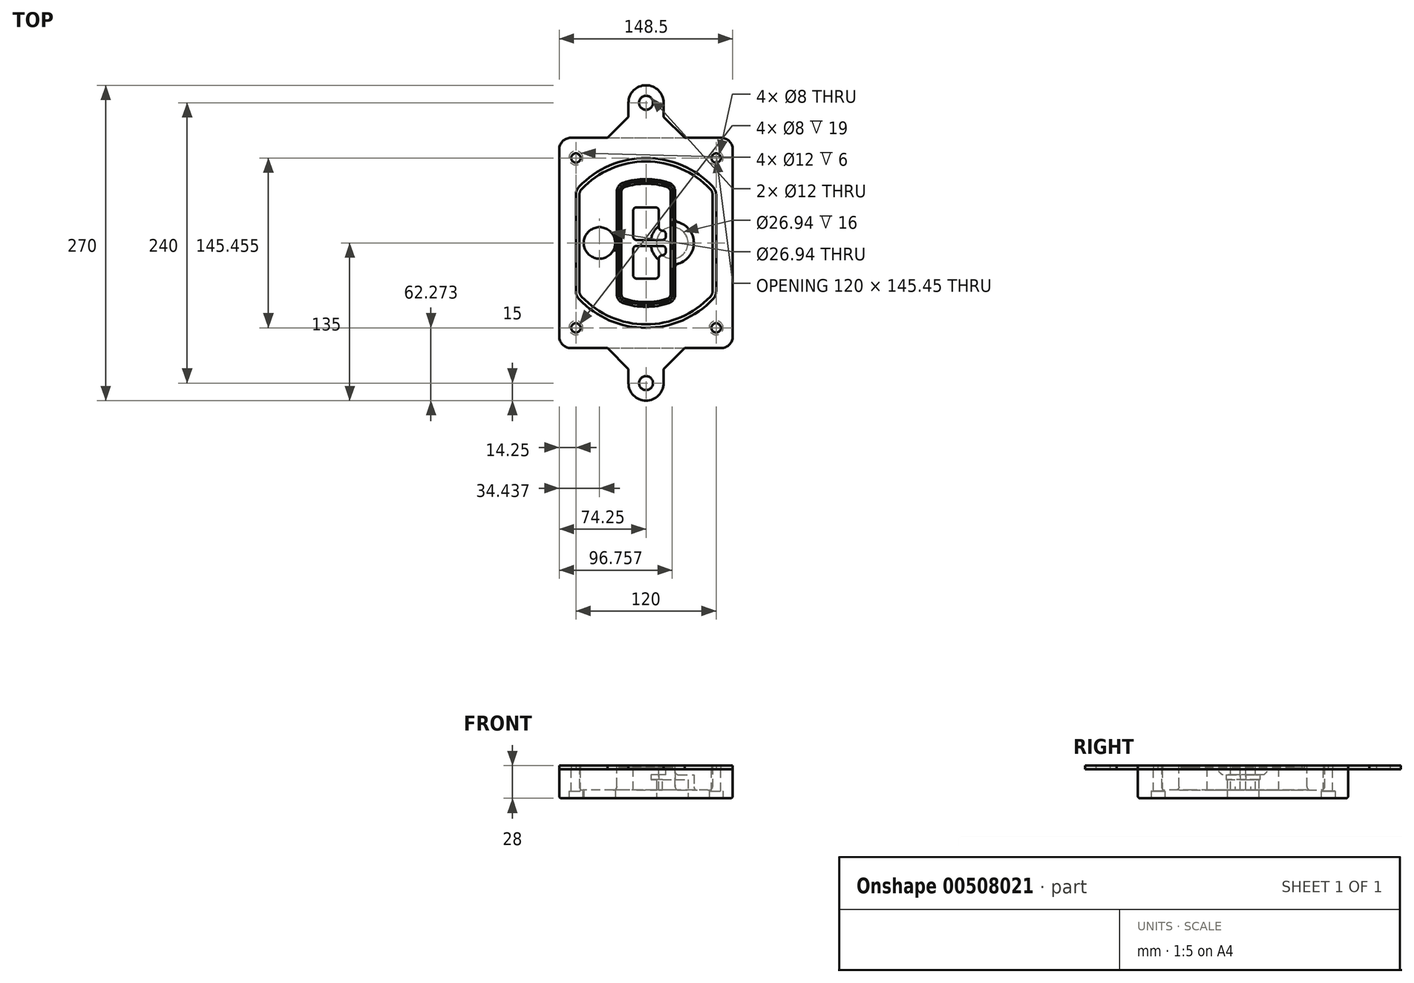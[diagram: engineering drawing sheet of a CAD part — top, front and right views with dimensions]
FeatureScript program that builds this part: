
annotation { "Feature Type Name" : "Feature", "Feature Type Description" : "" }
export const myFeature = defineFeature(function(context is Context, id is Id, definition is map)
    precondition{}
    {
        {
            var Q0;
            Q0=qCreatedBy(makeId("Top.planeOp"),FACE);
            var sketch = newSketch(context, id + "F0", { "sketchPlane" : qUnion([Q0])});
            skPoint(sketch, "E0.rect.middle", {"position": v(0, 0) * mm});
            skLineSegment(sketch, "E1.bottom", {"start": v(-64.25, -90) * mm, "end": v(64.25, -90) * mm});
            skLineSegment(sketch, "E1.top", {"start": v(-64.25, 90) * mm, "end": v(64.25, 90) * mm});
            skLineSegment(sketch, "E1.left", {"start": v(-74.25, -80) * mm, "end": v(-74.25, 80) * mm});
            skLineSegment(sketch, "E1.right", {"start": v(74.25, -80) * mm, "end": v(74.25, 80) * mm});
            skLineSegment(sketch, "E2", {"start": v(-74.25, 90) * mm, "end": v(74.25, -90) * mm, "construction": true});
            skLineSegment(sketch, "E3", {"start": v(74.25, 90) * mm, "end": v(-74.25, -90) * mm, "construction": true});
            skCircle(sketch, "E4", {"center": v(-60, 72.73) * mm, "radius": 4 * mm});
            skCircle(sketch, "E5", {"center": v(60, 72.73) * mm, "radius": 4 * mm});
            skCircle(sketch, "E6", {"center": v(60, -72.73) * mm, "radius": 4 * mm});
            skCircle(sketch, "E7", {"center": v(-60, -72.73) * mm, "radius": 4 * mm});
            skLineSegment(sketch, "E8", {"start": v(-60, 72.73) * mm, "end": v(60, 72.73) * mm, "construction": true});
            skLineSegment(sketch, "E9", {"start": v(60, 72.73) * mm, "end": v(60, -72.73) * mm, "construction": true});
            skLineSegment(sketch, "E10", {"start": v(60, -72.73) * mm, "end": v(-60, -72.73) * mm, "construction": true});
            skLineSegment(sketch, "E11", {"start": v(-60, -72.73) * mm, "end": v(-60, 72.73) * mm, "construction": true});
            skLineSegment(sketch, "E12", {"start": v(-60, 41.18) * mm, "end": v(-60, -41.18) * mm});
            skLineSegment(sketch, "E13", {"start": v(60, 41.18) * mm, "end": v(60, -41.18) * mm});
            skArc(sketch, "E14", {"start": v(57.27, 48.05) * mm, "mid": v(0, 72.73) * mm, "end": v(-57.27, 48.05) * mm});
            skArc(sketch, "E15", {"start": v(-57.27, -48.05) * mm, "mid": v(0, -72.73) * mm, "end": v(57.27, -48.05) * mm});
            skLineSegment(sketch, "E16", {"start": v(-60, 0) * mm, "end": v(60, 0) * mm, "construction": true});
            skPoint(sketch, "E17.visualSharp", {"position": v(-60, -45) * mm});
            skArc(sketch, "E17.filletArc", {"start": v(-60, -41.18) * mm, "mid": v(-59.3, -44.87) * mm, "end": v(-57.27, -48.05) * mm});
            skPoint(sketch, "E18.visualSharp", {"position": v(-60, 45) * mm});
            skArc(sketch, "E18.filletArc", {"start": v(-57.27, 48.05) * mm, "mid": v(-59.3, 44.87) * mm, "end": v(-60, 41.18) * mm});
            skPoint(sketch, "E19.visualSharp", {"position": v(60, 45) * mm});
            skArc(sketch, "E19.filletArc", {"start": v(60, 41.18) * mm, "mid": v(59.3, 44.87) * mm, "end": v(57.27, 48.05) * mm});
            skPoint(sketch, "E20.visualSharp", {"position": v(60, -45) * mm});
            skArc(sketch, "E20.filletArc", {"start": v(57.27, -48.05) * mm, "mid": v(59.3, -44.87) * mm, "end": v(60, -41.18) * mm});
            skPoint(sketch, "E21.visualSharp", {"position": v(-74.25, 90) * mm});
            skArc(sketch, "E21.filletArc", {"start": v(-64.25, 90) * mm, "mid": v(-71.32, 87.07) * mm, "end": v(-74.25, 80) * mm});
            skPoint(sketch, "E22.visualSharp", {"position": v(74.25, 90) * mm});
            skArc(sketch, "E22.filletArc", {"start": v(74.25, 80) * mm, "mid": v(71.32, 87.07) * mm, "end": v(64.25, 90) * mm});
            skPoint(sketch, "E23.visualSharp", {"position": v(74.25, -90) * mm});
            skArc(sketch, "E23.filletArc", {"start": v(64.25, -90) * mm, "mid": v(71.32, -87.07) * mm, "end": v(74.25, -80) * mm});
            skPoint(sketch, "E24.visualSharp", {"position": v(-74.25, -90) * mm});
            skArc(sketch, "E24.filletArc", {"start": v(-74.25, -80) * mm, "mid": v(-71.32, -87.07) * mm, "end": v(-64.25, -90) * mm});
            skArc(sketch, "E25.0", {"start": v(57, 41.18) * mm, "mid": v(56.5, 43.76) * mm, "end": v(55.09, 45.99) * mm});
            skLineSegment(sketch, "E25.1", {"start": v(57, 41.18) * mm, "end": v(57, -41.18) * mm});
            skArc(sketch, "E25.2", {"start": v(55.09, -45.99) * mm, "mid": v(56.5, -43.76) * mm, "end": v(57, -41.18) * mm});
            skArc(sketch, "E25.3", {"start": v(-55.09, -45.99) * mm, "mid": v(0, -69.73) * mm, "end": v(55.09, -45.99) * mm});
            skArc(sketch, "E25.4", {"start": v(-57, -41.18) * mm, "mid": v(-56.5, -43.76) * mm, "end": v(-55.09, -45.99) * mm});
            skArc(sketch, "E25.5", {"start": v(55.09, 45.99) * mm, "mid": v(0, 69.73) * mm, "end": v(-55.09, 45.99) * mm});
            skLineSegment(sketch, "E25.6", {"start": v(-57, 41.18) * mm, "end": v(-57, -41.18) * mm});
            skArc(sketch, "E25.7", {"start": v(-55.09, 45.99) * mm, "mid": v(-56.5, 43.76) * mm, "end": v(-57, 41.18) * mm});
            skArc(sketch, "E26.0", {"start": v(-60.18, 50.8) * mm, "mid": v(-63, 46.35) * mm, "end": v(-64, 41.18) * mm});
            skArc(sketch, "E26.1", {"start": v(60.18, 50.8) * mm, "mid": v(0, 76.73) * mm, "end": v(-60.18, 50.8) * mm});
            skArc(sketch, "E26.2", {"start": v(64, 41.18) * mm, "mid": v(63, 46.35) * mm, "end": v(60.18, 50.8) * mm});
            skLineSegment(sketch, "E26.3", {"start": v(64, 41.18) * mm, "end": v(64, -41.18) * mm});
            skArc(sketch, "E26.4", {"start": v(60.18, -50.8) * mm, "mid": v(63, -46.35) * mm, "end": v(64, -41.18) * mm});
            skLineSegment(sketch, "E26.5", {"start": v(-64, 41.18) * mm, "end": v(-64, -41.18) * mm});
            skArc(sketch, "E26.6", {"start": v(-60.18, -50.8) * mm, "mid": v(0, -76.73) * mm, "end": v(60.18, -50.8) * mm});
            skArc(sketch, "E26.7", {"start": v(-64, -41.18) * mm, "mid": v(-63, -46.35) * mm, "end": v(-60.18, -50.8) * mm});
            skSolve(sketch);
        }
        {
            var Q0;
            Q0=makeQuery(id+"F0.imprint","IMPRINT",FACE,{"disambiguationData":[TD([[makeQuery(id+"F0.imprint","IMPRINT",EDGE,{"derivedFrom":sQuery(id+"F0.wireOp",EDGE,"E1.bottom")}),1.0]])]});
            var Q1;
            Q1=makeQuery(id+"F0.imprint","IMPRINT",FACE,{"disambiguationData":[TD([[makeQuery(id+"F0.imprint","IMPRINT",EDGE,{"derivedFrom":sQuery(id+"F0.wireOp",EDGE,"E12")}),1.0]])]});
            var Q2;
            Q2=makeQuery(id+"F0.imprint","IMPRINT",FACE,{"disambiguationData":[TD([[makeQuery(id+"F0.imprint","IMPRINT",EDGE,{"derivedFrom":sQuery(id+"F0.wireOp",EDGE,"E25.0")}),1.0]])]});
            var Q3;
            Q3=makeQuery(id+"F0.imprint","IMPRINT",FACE,{"disambiguationData":[TD([[makeQuery(id+"F0.imprint","IMPRINT",EDGE,{"derivedFrom":sQuery(id+"F0.wireOp",EDGE,"E12")}),-1.0]])]});
            extrude(context, id + "F1", {"entities" : qUnion([Q0, Q1, Q2, Q3]), "oppositeDirection" : true, "depth" : 25 * mm});
        }
        {
            var Q0;
            Q0=makeQuery(id+"F0.imprint","IMPRINT",FACE,{"disambiguationData":[TD([[makeQuery(id+"F0.imprint","IMPRINT",EDGE,{"derivedFrom":sQuery(id+"F0.wireOp",EDGE,"E12")}),1.0]])]});
            extrude(context, id + "F2", {"entities" : qUnion([Q0]), "operationType" : NewBodyOperationType.ADD, "depth" : 3 * mm});
        }
        {
            var Q0;
            Q0=makeQuery(id+"F0.imprint","IMPRINT",FACE,{"disambiguationData":[TD([[makeQuery(id+"F0.imprint","IMPRINT",EDGE,{"derivedFrom":sQuery(id+"F0.wireOp",EDGE,"E25.0")}),1.0]])]});
            extrude(context, id + "F3", {"entities" : qUnion([Q0]), "operationType" : NewBodyOperationType.REMOVE, "oppositeDirection" : true, "depth" : 18 * mm});
        }
        {
            var Q0;
            Q0=makeQuery(id+"F2.opExtrude","CAP_FACE",FACE,{"disambiguationData":[OSD([sQuery(id+"F0.wireOp",EDGE,"E12"),sQuery(id+"F0.wireOp",EDGE,"E13"),sQuery(id+"F0.wireOp",EDGE,"E14"),sQuery(id+"F0.wireOp",EDGE,"E15"),sQuery(id+"F0.wireOp",EDGE,"E17.filletArc"),sQuery(id+"F0.wireOp",EDGE,"E18.filletArc"),sQuery(id+"F0.wireOp",EDGE,"E19.filletArc"),sQuery(id+"F0.wireOp",EDGE,"E20.filletArc"),sQuery(id+"F0.wireOp",EDGE,"E25.0"),sQuery(id+"F0.wireOp",EDGE,"E25.1"),sQuery(id+"F0.wireOp",EDGE,"E25.2"),sQuery(id+"F0.wireOp",EDGE,"E25.3"),sQuery(id+"F0.wireOp",EDGE,"E25.4"),sQuery(id+"F0.wireOp",EDGE,"E25.5"),sQuery(id+"F0.wireOp",EDGE,"E25.6"),sQuery(id+"F0.wireOp",EDGE,"E25.7")])],"isStart":false});
            var sketch = newSketch(context, id + "F4", { "sketchPlane" : qUnion([Q0])});
            skArc(sketch, "E27.0", {"start": v(-19.58, -51.49) * mm, "mid": v(0, -54.73) * mm, "end": v(19.58, -51.49) * mm});
            skArc(sketch, "E28.0", {"start": v(19.58, 51.49) * mm, "mid": v(0, 54.73) * mm, "end": v(-19.58, 51.49) * mm});
            skLineSegment(sketch, "E29", {"start": v(-25, 43.91) * mm, "end": v(-25, -43.91) * mm});
            skLineSegment(sketch, "E30", {"start": v(25, 43.91) * mm, "end": v(25, -43.91) * mm});
            skLineSegment(sketch, "E31", {"start": v(-25, 49.35) * mm, "end": v(25, 49.35) * mm, "construction": true});
            skLineSegment(sketch, "E32", {"start": v(-25, -49.35) * mm, "end": v(25, -49.35) * mm, "construction": true});
            skPoint(sketch, "E33.visualSharp", {"position": v(-25, 49.35) * mm});
            skArc(sketch, "E33.filletArc", {"start": v(-19.58, 51.49) * mm, "mid": v(-23.5, 48.57) * mm, "end": v(-25, 43.91) * mm});
            skPoint(sketch, "E34.visualSharp", {"position": v(25, 49.35) * mm});
            skArc(sketch, "E34.filletArc", {"start": v(25, 43.91) * mm, "mid": v(23.5, 48.57) * mm, "end": v(19.58, 51.49) * mm});
            skPoint(sketch, "E35.visualSharp", {"position": v(25, -49.35) * mm});
            skArc(sketch, "E35.filletArc", {"start": v(19.58, -51.49) * mm, "mid": v(23.5, -48.57) * mm, "end": v(25, -43.91) * mm});
            skPoint(sketch, "E36.visualSharp", {"position": v(-25, -49.35) * mm});
            skArc(sketch, "E36.filletArc", {"start": v(-25, -43.91) * mm, "mid": v(-23.5, -48.57) * mm, "end": v(-19.58, -51.49) * mm});
            skArc(sketch, "E37.0", {"start": v(55.09, 45.99) * mm, "mid": v(0, 69.73) * mm, "end": v(-55.09, 45.99) * mm});
            skArc(sketch, "E37.1", {"start": v(-55.09, 45.99) * mm, "mid": v(-56.5, 43.76) * mm, "end": v(-57, 41.18) * mm});
            skLineSegment(sketch, "E37.2", {"start": v(-57, 41.18) * mm, "end": v(-57, -41.18) * mm});
            skArc(sketch, "E37.3", {"start": v(-57, -41.18) * mm, "mid": v(-56.5, -43.76) * mm, "end": v(-55.09, -45.99) * mm});
            skArc(sketch, "E37.4", {"start": v(-55.09, -45.99) * mm, "mid": v(0, -69.73) * mm, "end": v(55.09, -45.99) * mm});
            skArc(sketch, "E37.5", {"start": v(55.09, -45.99) * mm, "mid": v(56.5, -43.76) * mm, "end": v(57, -41.18) * mm});
            skLineSegment(sketch, "E37.6", {"start": v(57, 41.18) * mm, "end": v(57, -41.18) * mm});
            skArc(sketch, "E37.7", {"start": v(57, 41.18) * mm, "mid": v(56.5, 43.76) * mm, "end": v(55.09, 45.99) * mm});
            skLineSegment(sketch, "E38.0", {"start": v(23, 43.91) * mm, "end": v(23, -43.91) * mm});
            skArc(sketch, "E38.1", {"start": v(18.93, -49.6) * mm, "mid": v(21.88, -47.4) * mm, "end": v(23, -43.91) * mm});
            skArc(sketch, "E38.2", {"start": v(-18.93, -49.6) * mm, "mid": v(0, -52.73) * mm, "end": v(18.93, -49.6) * mm});
            skArc(sketch, "E38.3", {"start": v(-23, -43.91) * mm, "mid": v(-21.88, -47.4) * mm, "end": v(-18.93, -49.6) * mm});
            skLineSegment(sketch, "E38.4", {"start": v(-23, 43.91) * mm, "end": v(-23, -43.91) * mm});
            skArc(sketch, "E38.5", {"start": v(23, 43.91) * mm, "mid": v(21.88, 47.4) * mm, "end": v(18.93, 49.6) * mm});
            skArc(sketch, "E38.6", {"start": v(-18.93, 49.6) * mm, "mid": v(-21.88, 47.4) * mm, "end": v(-23, 43.91) * mm});
            skArc(sketch, "E38.7", {"start": v(18.93, 49.6) * mm, "mid": v(0, 52.73) * mm, "end": v(-18.93, 49.6) * mm});
            skArc(sketch, "E39.0", {"start": v(21, 43.91) * mm, "mid": v(20.25, 46.24) * mm, "end": v(18.29, 47.7) * mm});
            skLineSegment(sketch, "E39.1", {"start": v(21, 43.91) * mm, "end": v(21, -43.91) * mm});
            skArc(sketch, "E39.2", {"start": v(18.29, -47.7) * mm, "mid": v(20.25, -46.24) * mm, "end": v(21, -43.91) * mm});
            skArc(sketch, "E39.3", {"start": v(-18.29, -47.7) * mm, "mid": v(0, -50.73) * mm, "end": v(18.29, -47.7) * mm});
            skArc(sketch, "E39.4", {"start": v(-21, -43.91) * mm, "mid": v(-20.25, -46.24) * mm, "end": v(-18.29, -47.7) * mm});
            skArc(sketch, "E39.5", {"start": v(18.29, 47.7) * mm, "mid": v(0, 50.73) * mm, "end": v(-18.29, 47.7) * mm});
            skLineSegment(sketch, "E39.6", {"start": v(-21, 43.91) * mm, "end": v(-21, -43.91) * mm});
            skArc(sketch, "E39.7", {"start": v(-18.29, 47.7) * mm, "mid": v(-20.25, 46.24) * mm, "end": v(-21, 43.91) * mm});
            skLineSegment(sketch, "E40", {"start": v(-25, 0) * mm, "end": v(25, 0) * mm, "construction": true});
            skLineSegment(sketch, "E41", {"start": v(-11, 5.5) * mm, "end": v(-11, 27.5) * mm});
            skLineSegment(sketch, "E42", {"start": v(-8, 30.5) * mm, "end": v(8, 30.5) * mm});
            skLineSegment(sketch, "E43", {"start": v(11, 27.5) * mm, "end": v(11, 13.5) * mm});
            skLineSegment(sketch, "E44", {"start": v(14, 10.5) * mm, "end": v(14, 10.5) * mm});
            skLineSegment(sketch, "E45", {"start": v(17, 7.5) * mm, "end": v(17, 5.5) * mm});
            skLineSegment(sketch, "E46", {"start": v(14, 2.5) * mm, "end": v(-8, 2.5) * mm});
            skPoint(sketch, "E47.visualSharp", {"position": v(-11, 30.5) * mm});
            skArc(sketch, "E47.filletArc", {"start": v(-8, 30.5) * mm, "mid": v(-10.12, 29.62) * mm, "end": v(-11, 27.5) * mm});
            skPoint(sketch, "E48.visualSharp", {"position": v(11, 30.5) * mm});
            skArc(sketch, "E48.filletArc", {"start": v(11, 27.5) * mm, "mid": v(10.12, 29.62) * mm, "end": v(8, 30.5) * mm});
            skPoint(sketch, "E49.visualSharp", {"position": v(11, 10.5) * mm});
            skArc(sketch, "E49.filletArc", {"start": v(11, 13.5) * mm, "mid": v(11.88, 11.38) * mm, "end": v(14, 10.5) * mm});
            skPoint(sketch, "E50.visualSharp", {"position": v(17, 10.5) * mm});
            skArc(sketch, "E50.filletArc", {"start": v(17, 7.5) * mm, "mid": v(16.12, 9.62) * mm, "end": v(14, 10.5) * mm});
            skPoint(sketch, "E51.visualSharp", {"position": v(17, 2.5) * mm});
            skArc(sketch, "E51.filletArc", {"start": v(14, 2.5) * mm, "mid": v(16.12, 3.38) * mm, "end": v(17, 5.5) * mm});
            skPoint(sketch, "E52.visualSharp", {"position": v(-11, 2.5) * mm});
            skArc(sketch, "E52.filletArc", {"start": v(-11, 5.5) * mm, "mid": v(-10.12, 3.38) * mm, "end": v(-8, 2.5) * mm});
            skLineSegment(sketch, "E53.0.MirrorCS", {"start": v(14, -2.5) * mm, "end": v(-8, -2.5) * mm});
            skArc(sketch, "E54.0.MirrorCS", {"start": v(-11, -5.5) * mm, "mid": v(-10.12, -3.38) * mm, "end": v(-8, -2.5) * mm});
            skLineSegment(sketch, "E55.0.MirrorCS", {"start": v(-11, -5.5) * mm, "end": v(-11, -27.5) * mm});
            skArc(sketch, "E56.0.MirrorCS", {"start": v(-8, -30.5) * mm, "mid": v(-10.12, -29.62) * mm, "end": v(-11, -27.5) * mm});
            skLineSegment(sketch, "E57.0.MirrorCS", {"start": v(-8, -30.5) * mm, "end": v(8, -30.5) * mm});
            skArc(sketch, "E58.0.MirrorCS", {"start": v(11, -27.5) * mm, "mid": v(10.12, -29.62) * mm, "end": v(8, -30.5) * mm});
            skLineSegment(sketch, "E59.0.MirrorCS", {"start": v(11, -27.5) * mm, "end": v(11, -13.5) * mm});
            skArc(sketch, "E60.0.MirrorCS", {"start": v(11, -13.5) * mm, "mid": v(11.88, -11.38) * mm, "end": v(14, -10.5) * mm});
            skArc(sketch, "E61.0.MirrorCS", {"start": v(17, -7.5) * mm, "mid": v(16.12, -9.62) * mm, "end": v(14, -10.5) * mm});
            skLineSegment(sketch, "E62.0.MirrorCS", {"start": v(17, -7.5) * mm, "end": v(17, -5.5) * mm});
            skArc(sketch, "E63.0.MirrorCS", {"start": v(14, -2.5) * mm, "mid": v(16.12, -3.38) * mm, "end": v(17, -5.5) * mm});
            skSolve(sketch);
        }
        {
            var Q0;
            Q0=makeQuery(id+"F4.imprint","IMPRINT",FACE,{"disambiguationData":[TD([[makeQuery(id+"F4.imprint","IMPRINT",EDGE,{"derivedFrom":sQuery(id+"F4.wireOp",EDGE,"E27.0")}),1.0]])]});
            var Q1;
            Q1=makeQuery(id+"F4.imprint","IMPRINT",FACE,{"disambiguationData":[TD([[makeQuery(id+"F4.imprint","IMPRINT",EDGE,{"derivedFrom":sQuery(id+"F4.wireOp",EDGE,"E38.0")}),-1.0]])]});
            var Q2;
            Q2=makeQuery(id+"F4.imprint","IMPRINT",FACE,{"disambiguationData":[TD([[makeQuery(id+"F4.imprint","IMPRINT",EDGE,{"derivedFrom":sQuery(id+"F4.wireOp",EDGE,"E39.0")}),1.0]])]});
            extrude(context, id + "F5", {"entities" : qUnion([Q0, Q1, Q2]), "operationType" : NewBodyOperationType.ADD, "endBound" : BoundingType.UP_TO_NEXT, "oppositeDirection" : true, "depth" : 25 * mm});
        }
        {
            var Q0;
            Q0=makeQuery(id+"F4.imprint","IMPRINT",FACE,{"disambiguationData":[TD([[makeQuery(id+"F4.imprint","IMPRINT",EDGE,{"derivedFrom":sQuery(id+"F4.wireOp",EDGE,"E38.0")}),-1.0]])]});
            extrude(context, id + "F6", {"entities" : qUnion([Q0]), "operationType" : NewBodyOperationType.REMOVE, "oppositeDirection" : true, "depth" : 2 * mm});
        }
        {
            var Q0;
            Q0=makeQuery(id+"F1.opExtrude","CAP_FACE",FACE,{"disambiguationData":[OSD([sQuery(id+"F0.wireOp",EDGE,"E1.bottom"),sQuery(id+"F0.wireOp",EDGE,"E1.top"),sQuery(id+"F0.wireOp",EDGE,"E1.left"),sQuery(id+"F0.wireOp",EDGE,"E1.right"),sQuery(id+"F0.wireOp",EDGE,"E4"),sQuery(id+"F0.wireOp",EDGE,"E5"),sQuery(id+"F0.wireOp",EDGE,"E6"),sQuery(id+"F0.wireOp",EDGE,"E7"),sQuery(id+"F0.wireOp",EDGE,"E21.filletArc"),sQuery(id+"F0.wireOp",EDGE,"E22.filletArc"),sQuery(id+"F0.wireOp",EDGE,"E23.filletArc"),sQuery(id+"F0.wireOp",EDGE,"E24.filletArc")])],"isStart":false});
            var sketch = newSketch(context, id + "F7", { "sketchPlane" : qUnion([Q0])});
            skCircle(sketch, "E64", {"center": v(22.5, 0) * mm, "radius": 13.47 * mm});
            skCircle(sketch, "E65", {"center": v(-39.81, 0) * mm, "radius": 13.47 * mm});
            skLineSegment(sketch, "E66", {"start": v(74.25, 0) * mm, "end": v(-74.25, 0) * mm});
            skCircle(sketch, "E67", {"center": v(22.5, 0) * mm, "radius": 18.47 * mm});
            skCircle(sketch, "E68", {"center": v(60, -72.73) * mm, "radius": 6 * mm});
            skCircle(sketch, "E69", {"center": v(-60, -72.73) * mm, "radius": 6 * mm});
            skCircle(sketch, "E70", {"center": v(-60, 72.73) * mm, "radius": 6 * mm});
            skCircle(sketch, "E71", {"center": v(60, 72.73) * mm, "radius": 6 * mm});
            skSolve(sketch);
        }
        {
            var Q0;
            {var subQ1=sQuery(id+"F7.wireOp",EDGE,"E66");var subQ4=sQuery(id+"F7.wireOp",EDGE,"E64");var subQ6=makeQuery(id+"F7.imprint","INTERSECT",VERTEX,{"disambiguationData":[OD(0.0)],"derivedFrom":[subQ4,subQ1]});Q0=makeQuery(id+"F7.imprint","IMPRINT",FACE,{"disambiguationData":[TD([[makeQuery(id+"F7.imprint","IMPRINT",EDGE,{"disambiguationData":[TD([[subQ6,-1.0]])],"derivedFrom":subQ4}),-1.0]])]});}
            var Q1;
            {var subQ0=sQuery(id+"F7.wireOp",EDGE,"E66");var subQ1=sQuery(id+"F7.wireOp",EDGE,"E64");var subQ3=makeQuery(id+"F7.imprint","INTERSECT",VERTEX,{"disambiguationData":[OD(0.0)],"derivedFrom":[subQ1,subQ0]});Q1=makeQuery(id+"F7.imprint","IMPRINT",FACE,{"disambiguationData":[TD([[makeQuery(id+"F7.imprint","IMPRINT",EDGE,{"disambiguationData":[TD([[subQ3,-1.0]])],"derivedFrom":subQ1}),1.0]])]});}
            var Q2;
            {var subQ0=sQuery(id+"F7.wireOp",EDGE,"E66");var subQ1=sQuery(id+"F7.wireOp",EDGE,"E64");var subQ3=makeQuery(id+"F7.imprint","INTERSECT",VERTEX,{"disambiguationData":[OD(0.0)],"derivedFrom":[subQ1,subQ0]});Q2=makeQuery(id+"F7.imprint","IMPRINT",FACE,{"disambiguationData":[TD([[makeQuery(id+"F7.imprint","IMPRINT",EDGE,{"disambiguationData":[TD([[subQ3,1.0]])],"derivedFrom":subQ1}),1.0]])]});}
            var Q3;
            {var subQ1=sQuery(id+"F7.wireOp",EDGE,"E66");var subQ4=sQuery(id+"F7.wireOp",EDGE,"E64");var subQ6=makeQuery(id+"F7.imprint","INTERSECT",VERTEX,{"disambiguationData":[OD(0.0)],"derivedFrom":[subQ4,subQ1]});Q3=makeQuery(id+"F7.imprint","IMPRINT",FACE,{"disambiguationData":[TD([[makeQuery(id+"F7.imprint","IMPRINT",EDGE,{"disambiguationData":[TD([[subQ6,1.0]])],"derivedFrom":subQ4}),-1.0]])]});}
            extrude(context, id + "F8", {"entities" : qUnion([Q0, Q1, Q2, Q3]), "operationType" : NewBodyOperationType.ADD, "oppositeDirection" : true, "depth" : 20 * mm});
        }
        {
            var Q0;
            {var subQ0=sQuery(id+"F7.wireOp",EDGE,"E66");var subQ1=sQuery(id+"F7.wireOp",EDGE,"E64");var subQ3=makeQuery(id+"F7.imprint","INTERSECT",VERTEX,{"disambiguationData":[OD(0.0)],"derivedFrom":[subQ1,subQ0]});Q0=makeQuery(id+"F7.imprint","IMPRINT",FACE,{"disambiguationData":[TD([[makeQuery(id+"F7.imprint","IMPRINT",EDGE,{"disambiguationData":[TD([[subQ3,-1.0]])],"derivedFrom":subQ1}),1.0]])]});}
            var Q1;
            {var subQ0=sQuery(id+"F7.wireOp",EDGE,"E66");var subQ1=sQuery(id+"F7.wireOp",EDGE,"E64");var subQ3=makeQuery(id+"F7.imprint","INTERSECT",VERTEX,{"disambiguationData":[OD(0.0)],"derivedFrom":[subQ1,subQ0]});Q1=makeQuery(id+"F7.imprint","IMPRINT",FACE,{"disambiguationData":[TD([[makeQuery(id+"F7.imprint","IMPRINT",EDGE,{"disambiguationData":[TD([[subQ3,1.0]])],"derivedFrom":subQ1}),1.0]])]});}
            extrude(context, id + "F9", {"entities" : qUnion([Q0, Q1]), "operationType" : NewBodyOperationType.REMOVE, "oppositeDirection" : true, "depth" : 16 * mm});
        }
        {
            var Q0;
            {var subQ0=sQuery(id+"F7.wireOp",EDGE,"E66");var subQ1=sQuery(id+"F7.wireOp",EDGE,"E65");var subQ3=makeQuery(id+"F7.imprint","INTERSECT",VERTEX,{"disambiguationData":[OD(0.0)],"derivedFrom":[subQ1,subQ0]});Q0=makeQuery(id+"F7.imprint","IMPRINT",FACE,{"disambiguationData":[TD([[makeQuery(id+"F7.imprint","IMPRINT",EDGE,{"disambiguationData":[TD([[subQ3,-1.0]])],"derivedFrom":subQ1}),1.0]])]});}
            var Q1;
            {var subQ0=sQuery(id+"F7.wireOp",EDGE,"E66");var subQ1=sQuery(id+"F7.wireOp",EDGE,"E65");var subQ3=makeQuery(id+"F7.imprint","INTERSECT",VERTEX,{"disambiguationData":[OD(0.0)],"derivedFrom":[subQ1,subQ0]});Q1=makeQuery(id+"F7.imprint","IMPRINT",FACE,{"disambiguationData":[TD([[makeQuery(id+"F7.imprint","IMPRINT",EDGE,{"disambiguationData":[TD([[subQ3,1.0]])],"derivedFrom":subQ1}),1.0]])]});}
            extrude(context, id + "F10", {"entities" : qUnion([Q0, Q1]), "operationType" : NewBodyOperationType.REMOVE, "oppositeDirection" : true, "depth" : 25 * mm});
        }
        {
            var Q0;
            Q0=makeQuery(id+"F7.imprint","IMPRINT",FACE,{"disambiguationData":[TD([[makeQuery(id+"F7.imprint","IMPRINT",EDGE,{"derivedFrom":sQuery(id+"F7.wireOp",EDGE,"E68")}),1.0]])]});
            var Q1;
            Q1=makeQuery(id+"F7.imprint","IMPRINT",FACE,{"disambiguationData":[TD([[makeQuery(id+"F7.imprint","IMPRINT",EDGE,{"derivedFrom":makeQuery(id+"F1.opExtrude","CAP_EDGE",EDGE,{"disambiguationData":[OSD([sQuery(id+"F0.wireOp",EDGE,"E5")])],"isStart":false})}),-1.0]])]});
            var Q2;
            Q2=makeQuery(id+"F7.imprint","IMPRINT",FACE,{"disambiguationData":[TD([[makeQuery(id+"F7.imprint","IMPRINT",EDGE,{"derivedFrom":sQuery(id+"F7.wireOp",EDGE,"E69")}),1.0]])]});
            var Q3;
            Q3=makeQuery(id+"F7.imprint","IMPRINT",FACE,{"disambiguationData":[TD([[makeQuery(id+"F7.imprint","IMPRINT",EDGE,{"derivedFrom":makeQuery(id+"F1.opExtrude","CAP_EDGE",EDGE,{"disambiguationData":[OSD([sQuery(id+"F0.wireOp",EDGE,"E4")])],"isStart":false})}),-1.0]])]});
            var Q4;
            Q4=makeQuery(id+"F7.imprint","IMPRINT",FACE,{"disambiguationData":[TD([[makeQuery(id+"F7.imprint","IMPRINT",EDGE,{"derivedFrom":sQuery(id+"F7.wireOp",EDGE,"E70")}),1.0]])]});
            var Q5;
            Q5=makeQuery(id+"F7.imprint","IMPRINT",FACE,{"disambiguationData":[TD([[makeQuery(id+"F7.imprint","IMPRINT",EDGE,{"derivedFrom":makeQuery(id+"F1.opExtrude","CAP_EDGE",EDGE,{"disambiguationData":[OSD([sQuery(id+"F0.wireOp",EDGE,"E7")])],"isStart":false})}),-1.0]])]});
            var Q6;
            Q6=makeQuery(id+"F7.imprint","IMPRINT",FACE,{"disambiguationData":[TD([[makeQuery(id+"F7.imprint","IMPRINT",EDGE,{"derivedFrom":sQuery(id+"F7.wireOp",EDGE,"E71")}),1.0]])]});
            var Q7;
            Q7=makeQuery(id+"F7.imprint","IMPRINT",FACE,{"disambiguationData":[TD([[makeQuery(id+"F7.imprint","IMPRINT",EDGE,{"derivedFrom":makeQuery(id+"F1.opExtrude","CAP_EDGE",EDGE,{"disambiguationData":[OSD([sQuery(id+"F0.wireOp",EDGE,"E6")])],"isStart":false})}),-1.0]])]});
            extrude(context, id + "F11", {"entities" : qUnion([Q0, Q1, Q2, Q3, Q4, Q5, Q6, Q7]), "operationType" : NewBodyOperationType.REMOVE, "oppositeDirection" : true, "depth" : 6 * mm});
        }
        {
            var Q0;
            Q0=makeQuery(id+"F9.boolean.opBoolean","COPY",FACE,{"derivedFrom":makeQuery(id+"F9.opExtrude","CAP_FACE",FACE,{"disambiguationData":[OSD([sQuery(id+"F7.wireOp",EDGE,"E64")])],"isStart":false})});
            var sketch = newSketch(context, id + "F12", { "sketchPlane" : qUnion([Q0])});
            skArc(sketch, "E72.0", {"start": v(11, 14.45) * mm, "mid": v(6.45, 9.13) * mm, "end": v(4.2, 2.5) * mm});
            skArc(sketch, "E72.1", {"start": v(4.2, -2.5) * mm, "mid": v(6.45, -9.13) * mm, "end": v(11, -14.45) * mm});
            skLineSegment(sketch, "E73", {"start": v(4.2, -2.5) * mm, "end": v(14, -2.5) * mm});
            skLineSegment(sketch, "E74.0", {"start": v(14, 2.5) * mm, "end": v(4.2, 2.5) * mm});
            skArc(sketch, "E74.1", {"start": v(14, 2.5) * mm, "mid": v(16.12, 3.38) * mm, "end": v(17, 5.5) * mm});
            skLineSegment(sketch, "E74.2", {"start": v(17, 7.5) * mm, "end": v(17, 5.5) * mm});
            skArc(sketch, "E74.3", {"start": v(17, 7.5) * mm, "mid": v(16.12, 9.62) * mm, "end": v(14, 10.5) * mm});
            skArc(sketch, "E74.4", {"start": v(11, 13.5) * mm, "mid": v(11.88, 11.38) * mm, "end": v(14, 10.5) * mm});
            skLineSegment(sketch, "E74.5", {"start": v(11, 14.45) * mm, "end": v(11, 13.5) * mm});
            skLineSegment(sketch, "E74.7", {"start": v(14, -2.5) * mm, "end": v(4.2, -2.5) * mm});
            skArc(sketch, "E74.8", {"start": v(14, -2.5) * mm, "mid": v(16.12, -3.38) * mm, "end": v(17, -5.5) * mm});
            skLineSegment(sketch, "E74.9", {"start": v(17, -7.5) * mm, "end": v(17, -5.5) * mm});
            skArc(sketch, "E74.10", {"start": v(17, -7.5) * mm, "mid": v(16.12, -9.62) * mm, "end": v(14, -10.5) * mm});
            skArc(sketch, "E74.11", {"start": v(11, -13.5) * mm, "mid": v(11.88, -11.38) * mm, "end": v(14, -10.5) * mm});
            skLineSegment(sketch, "E74.12", {"start": v(11, -14.45) * mm, "end": v(11, -13.5) * mm});
            skPoint(sketch, "E75.orphan", {"position": v(11, -27.5) * mm});
            skPoint(sketch, "E76.orphan", {"position": v(-8, -2.5) * mm});
            skPoint(sketch, "E77.orphan", {"position": v(-8, 2.5) * mm});
            skPoint(sketch, "E78.orphan", {"position": v(11, 27.5) * mm});
            skSolve(sketch);
        }
        {
            var Q0;
            {var subQ7=sQuery(id+"F12.wireOp",EDGE,"E72.0");var subQ14=sQuery(id+"F12.wireOp",EDGE,"E72.1");var subQ16=sQuery(id+"F12.wireOp",EDGE,"E74.1");var subQ18=sQuery(id+"F12.wireOp",EDGE,"E74.8");Q0=qUnion([makeQuery(id+"F12.imprint","IMPRINT",FACE,{"disambiguationData":[TD([[makeQuery(id+"F12.imprint","IMPRINT",EDGE,{"derivedFrom":subQ7}),1.0]])]}),makeQuery(id+"F12.imprint","IMPRINT",FACE,{"disambiguationData":[TD([[makeQuery(id+"F12.imprint","IMPRINT",EDGE,{"derivedFrom":subQ14}),1.0]])]}),makeQuery(id+"F12.imprint","IMPRINT",FACE,{"disambiguationData":[TD([[makeQuery(id+"F12.imprint","IMPRINT",EDGE,{"derivedFrom":subQ16}),1.0]])]}),makeQuery(id+"F12.imprint","IMPRINT",FACE,{"disambiguationData":[TD([[makeQuery(id+"F12.imprint","IMPRINT",EDGE,{"derivedFrom":subQ18}),-1.0]])]})]);}
            var Q1;
            Q1=makeQuery(id+"F5.boolean.opBoolean","SPLIT",FACE,{"disambiguationData":[TD([makeQuery(id+"F5.opExtrude","SWEPT_FACE",FACE,{"disambiguationData":[OSD([sQuery(id+"F4.wireOp",EDGE,"E41")])]})])],"derivedFrom":makeQuery(id+"F3.boolean.opBoolean","COPY",FACE,{"derivedFrom":makeQuery(id+"F3.opExtrude","CAP_FACE",FACE,{"disambiguationData":[OSD([sQuery(id+"F0.wireOp",EDGE,"E25.0"),sQuery(id+"F0.wireOp",EDGE,"E25.1"),sQuery(id+"F0.wireOp",EDGE,"E25.2"),sQuery(id+"F0.wireOp",EDGE,"E25.3"),sQuery(id+"F0.wireOp",EDGE,"E25.4"),sQuery(id+"F0.wireOp",EDGE,"E25.5"),sQuery(id+"F0.wireOp",EDGE,"E25.6"),sQuery(id+"F0.wireOp",EDGE,"E25.7")])],"isStart":false})})});
            extrude(context, id + "F13", {"entities" : qUnion([Q0]), "operationType" : NewBodyOperationType.REMOVE, "endBound" : BoundingType.UP_TO_SURFACE, "endBoundEntityFace" : qUnion([Q1]), "depth" : 25 * mm});
        }
        {
            var Q0;
            Q0=makeQuery(id+"F3.boolean.opBoolean","COPY",EDGE,{"derivedFrom":makeQuery(id+"F3.opExtrude","CAP_EDGE",EDGE,{"disambiguationData":[OSD([sQuery(id+"F0.wireOp",EDGE,"E25.6")])],"isStart":false})});
            var Q1;
            Q1=makeQuery(id+"F8.boolean.opBoolean","INTERSECT",EDGE,{"derivedFrom":[makeQuery(id+"F5.opExtrude","SWEPT_FACE",FACE,{"disambiguationData":[OSD([sQuery(id+"F4.wireOp",EDGE,"E30")])]}),makeQuery(id+"F8.opExtrude","CAP_FACE",FACE,{"disambiguationData":[OSD([sQuery(id+"F7.wireOp",EDGE,"E67")])],"isStart":false})]});
            var Q2;
            Q2=makeQuery(id+"F8.boolean.opBoolean","INTERSECT",EDGE,{"disambiguationData":[OD(1.0)],"derivedFrom":[makeQuery(id+"F5.opExtrude","SWEPT_FACE",FACE,{"disambiguationData":[OSD([sQuery(id+"F4.wireOp",EDGE,"E30")])]}),makeQuery(id+"F8.opExtrude","SWEPT_FACE",FACE,{"disambiguationData":[OSD([sQuery(id+"F7.wireOp",EDGE,"E67")])]})]});
            var Q3;
            {var subQ0=sQuery(id+"F4.wireOp",EDGE,"E30");Q3=makeQuery(id+"F8.boolean.opBoolean","SPLIT",EDGE,{"disambiguationData":[TD([makeQuery(id+"F5.opExtrude","SWEPT_FACE",FACE,{"disambiguationData":[OSD([sQuery(id+"F4.wireOp",EDGE,"E35.filletArc")])]})])],"derivedFrom":makeQuery(id+"F5.opExtrude","CAP_EDGE",EDGE,{"disambiguationData":[OSD([subQ0])],"isStart":false})});}
            var Q4;
            {var subQ0=sQuery(id+"F0.wireOp",EDGE,"E25.7");var subQ1=sQuery(id+"F0.wireOp",EDGE,"E25.1");var subQ2=sQuery(id+"F0.wireOp",EDGE,"E25.6");var subQ3=sQuery(id+"F0.wireOp",EDGE,"E25.5");var subQ4=sQuery(id+"F0.wireOp",EDGE,"E25.4");var subQ5=sQuery(id+"F0.wireOp",EDGE,"E25.0");var subQ6=sQuery(id+"F0.wireOp",EDGE,"E25.2");var subQ7=sQuery(id+"F0.wireOp",EDGE,"E25.3");Q4=makeQuery(id+"F8.boolean.opBoolean","INTERSECT",EDGE,{"derivedFrom":[makeQuery(id+"F5.boolean.opBoolean","SPLIT",FACE,{"disambiguationData":[TD([makeQuery(id+"F2.opExtrude","SWEPT_FACE",FACE,{"disambiguationData":[OSD([subQ5])]})])],"derivedFrom":makeQuery(id+"F3.boolean.opBoolean","COPY",FACE,{"derivedFrom":makeQuery(id+"F3.opExtrude","CAP_FACE",FACE,{"disambiguationData":[OSD([subQ5,subQ1,subQ6,subQ7,subQ4,subQ3,subQ2,subQ0])],"isStart":false})})}),makeQuery(id+"F8.opExtrude","SWEPT_FACE",FACE,{"disambiguationData":[OSD([sQuery(id+"F7.wireOp",EDGE,"E67")])]})]});}
            var Q5;
            Q5=makeQuery(id+"F8.boolean.opBoolean","INTERSECT",EDGE,{"disambiguationData":[OD(0.0)],"derivedFrom":[makeQuery(id+"F5.opExtrude","SWEPT_FACE",FACE,{"disambiguationData":[OSD([sQuery(id+"F4.wireOp",EDGE,"E30")])]}),makeQuery(id+"F8.opExtrude","SWEPT_FACE",FACE,{"disambiguationData":[OSD([sQuery(id+"F7.wireOp",EDGE,"E67")])]})]});
            fillet(context, id + "F14", {"entities" : qUnion([Q0, Q1, Q2, Q3, Q4, Q5]), "radius" : 3 * mm, "tangentPropagation" : true, "allowEdgeOverflow" : false});
        }
        {
            var Q0;
            Q0=makeQuery(id+"F1.opExtrude","CAP_EDGE",EDGE,{"disambiguationData":[OSD([sQuery(id+"F0.wireOp",EDGE,"E1.bottom")])],"isStart":false});
            fillet(context, id + "F15", {"entities" : qUnion([Q0]), "radius" : 2 * mm, "tangentPropagation" : true, "allowEdgeOverflow" : false});
        }
        {
            var Q0;
            {var subQ0=sQuery(id+"F0.wireOp",EDGE,"E21.filletArc");var subQ1=sQuery(id+"F0.wireOp",EDGE,"E7");var subQ2=sQuery(id+"F0.wireOp",EDGE,"E6");var subQ3=sQuery(id+"F0.wireOp",EDGE,"E5");var subQ4=sQuery(id+"F0.wireOp",EDGE,"E4");var subQ5=sQuery(id+"F0.wireOp",EDGE,"E22.filletArc");var subQ6=sQuery(id+"F0.wireOp",EDGE,"E1.bottom");var subQ7=sQuery(id+"F0.wireOp",EDGE,"E1.right");var subQ8=sQuery(id+"F0.wireOp",EDGE,"E1.top");var subQ9=sQuery(id+"F0.wireOp",EDGE,"E1.left");var subQ10=sQuery(id+"F0.wireOp",EDGE,"E23.filletArc");var subQ11=sQuery(id+"F0.wireOp",EDGE,"E24.filletArc");Q0=makeQuery(id+"F2.boolean.opBoolean","SPLIT",FACE,{"disambiguationData":[TD([makeQuery(id+"F1.opExtrude","SWEPT_FACE",FACE,{"disambiguationData":[OSD([subQ6])]})])],"derivedFrom":makeQuery(id+"F1.opExtrude","CAP_FACE",FACE,{"disambiguationData":[OSD([subQ6,subQ8,subQ9,subQ7,subQ4,subQ3,subQ2,subQ1,subQ0,subQ5,subQ10,subQ11])],"isStart":true})});}
            var sketch = newSketch(context, id + "F16", { "sketchPlane" : qUnion([Q0])});
            skArc(sketch, "E79.0", {"start": v(57.27, 48.05) * mm, "mid": v(0, 72.73) * mm, "end": v(-57.27, 48.05) * mm});
            skLineSegment(sketch, "E79.1", {"start": v(60, 41.18) * mm, "end": v(60, -41.18) * mm});
            skArc(sketch, "E79.2", {"start": v(60, 41.18) * mm, "mid": v(59.3, 44.87) * mm, "end": v(57.27, 48.05) * mm});
            skArc(sketch, "E79.3", {"start": v(57.27, -48.05) * mm, "mid": v(59.3, -44.87) * mm, "end": v(60, -41.18) * mm});
            skArc(sketch, "E79.4", {"start": v(-57.27, -48.05) * mm, "mid": v(0, -72.73) * mm, "end": v(57.27, -48.05) * mm});
            skArc(sketch, "E79.5", {"start": v(-60, -41.18) * mm, "mid": v(-59.3, -44.87) * mm, "end": v(-57.27, -48.05) * mm});
            skLineSegment(sketch, "E79.6", {"start": v(-60, 41.18) * mm, "end": v(-60, -41.18) * mm});
            skArc(sketch, "E79.7", {"start": v(-57.27, 48.05) * mm, "mid": v(-59.3, 44.87) * mm, "end": v(-60, 41.18) * mm});
            skArc(sketch, "E79.8", {"start": v(74.25, 80) * mm, "mid": v(71.32, 87.07) * mm, "end": v(64.25, 90) * mm});
            skLineSegment(sketch, "E79.9", {"start": v(74.25, -80) * mm, "end": v(74.25, 80) * mm});
            skArc(sketch, "E79.10", {"start": v(64.25, -90) * mm, "mid": v(71.32, -87.07) * mm, "end": v(74.25, -80) * mm});
            skLineSegment(sketch, "E79.11", {"start": v(-64.25, -90) * mm, "end": v(64.25, -90) * mm});
            skLineSegment(sketch, "E79.12", {"start": v(-74.25, -80) * mm, "end": v(-74.25, 80) * mm});
            skArc(sketch, "E79.13", {"start": v(-74.25, -80) * mm, "mid": v(-71.32, -87.07) * mm, "end": v(-64.25, -90) * mm});
            skArc(sketch, "E79.14", {"start": v(-64.25, 90) * mm, "mid": v(-71.32, 87.07) * mm, "end": v(-74.25, 80) * mm});
            skLineSegment(sketch, "E79.15", {"start": v(-64.25, 90) * mm, "end": v(64.25, 90) * mm});
            skCircle(sketch, "E80.0", {"center": v(-60, 72.73) * mm, "radius": 4 * mm});
            skCircle(sketch, "E80.1", {"center": v(-60, -72.73) * mm, "radius": 4 * mm});
            skCircle(sketch, "E80.2", {"center": v(60, 72.73) * mm, "radius": 4 * mm});
            skCircle(sketch, "E80.3", {"center": v(60, -72.73) * mm, "radius": 4 * mm});
            skLineSegment(sketch, "E81", {"start": v(0, 90) * mm, "end": v(0, 120) * mm, "construction": true});
            skLineSegment(sketch, "E82", {"start": v(-33, 90) * mm, "end": v(-15, 108) * mm});
            skLineSegment(sketch, "E83", {"start": v(-15, 108) * mm, "end": v(-15, 120) * mm});
            skArc(sketch, "E84", {"start": v(-15, 120) * mm, "mid": v(0, 135) * mm, "end": v(15, 120) * mm});
            skCircle(sketch, "E85", {"center": v(0, 120) * mm, "radius": 6 * mm});
            skLineSegment(sketch, "E86", {"start": v(15, 120) * mm, "end": v(15, 108) * mm});
            skLineSegment(sketch, "E87", {"start": v(15, 108) * mm, "end": v(33, 90) * mm});
            skLineSegment(sketch, "E88", {"start": v(74.25, 0) * mm, "end": v(-74.25, 0) * mm, "construction": true});
            skLineSegment(sketch, "E89.MirrorCS", {"start": v(-33, -90) * mm, "end": v(-15, -108) * mm});
            skLineSegment(sketch, "E90.MirrorCS", {"start": v(-15, -108) * mm, "end": v(-15, -120) * mm});
            skArc(sketch, "E91.MirrorCS", {"start": v(-15, -120) * mm, "mid": v(0, -135) * mm, "end": v(15, -120) * mm});
            skLineSegment(sketch, "E92.MirrorCS", {"start": v(15, -120) * mm, "end": v(15, -108) * mm});
            skLineSegment(sketch, "E93.MirrorCS", {"start": v(15, -108) * mm, "end": v(33, -90) * mm});
            skCircle(sketch, "E94.MirrorC", {"center": v(0, -120) * mm, "radius": 6 * mm});
            skLineSegment(sketch, "E95.MirrorCS", {"start": v(0, -90) * mm, "end": v(0, -120) * mm, "construction": true});
            skSolve(sketch);
        }
        {
            var Q0;
            {var subQ0=sQuery(id+"F16.wireOp",EDGE,"E89.MirrorCS");Q0=makeQuery(id+"F16.imprint","IMPRINT",FACE,{"disambiguationData":[TD([[makeQuery(id+"F16.imprint","IMPRINT",EDGE,{"derivedFrom":subQ0}),1.0]])]});}
            var Q1;
            Q1=makeQuery(id+"F16.imprint","IMPRINT",FACE,{"disambiguationData":[TD([[makeQuery(id+"F16.imprint","IMPRINT",EDGE,{"derivedFrom":sQuery(id+"F16.wireOp",EDGE,"E79.0")}),-1.0]])]});
            var Q2;
            {var subQ0=sQuery(id+"F16.wireOp",EDGE,"E82");Q2=makeQuery(id+"F16.imprint","IMPRINT",FACE,{"disambiguationData":[TD([[makeQuery(id+"F16.imprint","IMPRINT",EDGE,{"derivedFrom":subQ0}),-1.0]])]});}
            var Q3;
            Q3=makeQuery(id+"F2.opExtrude","CAP_FACE",FACE,{"disambiguationData":[OSD([sQuery(id+"F0.wireOp",EDGE,"E12"),sQuery(id+"F0.wireOp",EDGE,"E13"),sQuery(id+"F0.wireOp",EDGE,"E14"),sQuery(id+"F0.wireOp",EDGE,"E15"),sQuery(id+"F0.wireOp",EDGE,"E17.filletArc"),sQuery(id+"F0.wireOp",EDGE,"E18.filletArc"),sQuery(id+"F0.wireOp",EDGE,"E19.filletArc"),sQuery(id+"F0.wireOp",EDGE,"E20.filletArc"),sQuery(id+"F0.wireOp",EDGE,"E25.0"),sQuery(id+"F0.wireOp",EDGE,"E25.1"),sQuery(id+"F0.wireOp",EDGE,"E25.2"),sQuery(id+"F0.wireOp",EDGE,"E25.3"),sQuery(id+"F0.wireOp",EDGE,"E25.4"),sQuery(id+"F0.wireOp",EDGE,"E25.5"),sQuery(id+"F0.wireOp",EDGE,"E25.6"),sQuery(id+"F0.wireOp",EDGE,"E25.7")])],"isStart":false});
            extrude(context, id + "F17", {"entities" : qUnion([Q0, Q1, Q2]), "endBound" : BoundingType.UP_TO_SURFACE, "endBoundEntityFace" : qUnion([Q3]), "depth" : 25 * mm});
        }
    });
